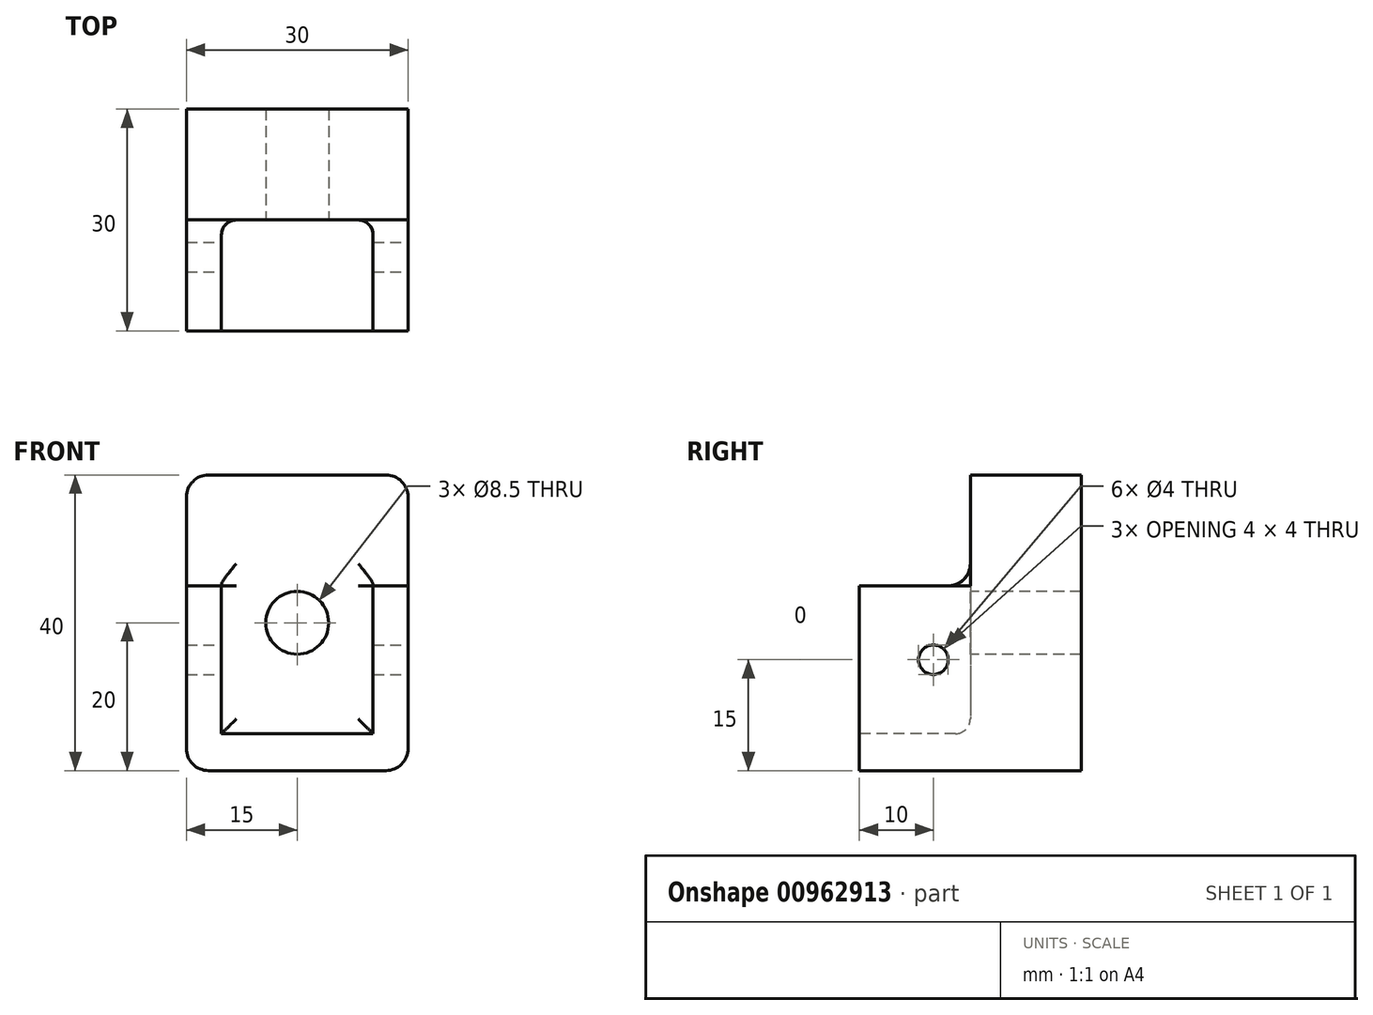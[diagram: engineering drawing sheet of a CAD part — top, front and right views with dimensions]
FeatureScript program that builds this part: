
annotation { "Feature Type Name" : "Feature", "Feature Type Description" : "" }
export const myFeature = defineFeature(function(context is Context, id is Id, definition is map)
    precondition{}
    {
        {
            var Q0;
            Q0=qCreatedBy(makeId("Front.planeOp"),FACE);
            var sketch = newSketch(context, id + "F0", { "sketchPlane" : qUnion([Q0])});
            skLineSegment(sketch, "E0.bottom", {"start": v(-15, 20) * mm, "end": v(15, 20) * mm});
            skLineSegment(sketch, "E0.top", {"start": v(-15, -20) * mm, "end": v(15, -20) * mm});
            skLineSegment(sketch, "E0.left", {"start": v(-15, 20) * mm, "end": v(-15, -20) * mm});
            skLineSegment(sketch, "E0.right", {"start": v(15, 20) * mm, "end": v(15, -20) * mm});
            skPoint(sketch, "E0.middle", {"position": v(0, 0) * mm});
            skSolve(sketch);
        }
        {
            var Q0;
            Q0 = qSketchRegion(id + "F0", true);
            extrude(context, id + "F1", {"entities" : qUnion([Q0]), "depth" : 30 * mm, "offsetDistance" : 25 * mm});
        }
        {
            var Q0;
            Q0=makeQuery(id+"F1.opExtrude","CAP_FACE",FACE,{"disambiguationData":[OSD([sQuery(id+"F0.wireOp",EDGE,"E0.bottom"),sQuery(id+"F0.wireOp",EDGE,"E0.top"),sQuery(id+"F0.wireOp",EDGE,"E0.left"),sQuery(id+"F0.wireOp",EDGE,"E0.right")])],"isStart":false});
            var sketch = newSketch(context, id + "F2", { "sketchPlane" : qUnion([Q0])});
            skLineSegment(sketch, "E1.bottom", {"start": v(-10.25, 15) * mm, "end": v(10.25, 15) * mm});
            skLineSegment(sketch, "E1.top", {"start": v(-10.25, -15) * mm, "end": v(10.25, -15) * mm});
            skLineSegment(sketch, "E1.left", {"start": v(-10.25, 15) * mm, "end": v(-10.25, -15) * mm});
            skLineSegment(sketch, "E1.right", {"start": v(10.25, 15) * mm, "end": v(10.25, -15) * mm});
            skPoint(sketch, "E1.middle", {"position": v(0, 0) * mm});
            skSolve(sketch);
        }
        {
            var Q0;
            Q0 = qSketchRegion(id + "F2", true);
            extrude(context, id + "F3", {"entities" : qUnion([Q0]), "operationType" : NewBodyOperationType.REMOVE, "oppositeDirection" : true, "depth" : 15 * mm, "offsetDistance" : 25 * mm});
        }
        {
            var Q0;
            Q0=makeQuery(id+"F1.opExtrude","CAP_FACE",FACE,{"disambiguationData":[OSD([sQuery(id+"F0.wireOp",EDGE,"E0.bottom"),sQuery(id+"F0.wireOp",EDGE,"E0.top"),sQuery(id+"F0.wireOp",EDGE,"E0.left"),sQuery(id+"F0.wireOp",EDGE,"E0.right")])],"isStart":false});
            var sketch = newSketch(context, id + "F4", { "sketchPlane" : qUnion([Q0])});
            skLineSegment(sketch, "E2.bottom", {"start": v(-15, 20) * mm, "end": v(19.05, 20) * mm});
            skLineSegment(sketch, "E2.top", {"start": v(-15, 5) * mm, "end": v(19.05, 5) * mm});
            skLineSegment(sketch, "E2.left", {"start": v(-15, 20) * mm, "end": v(-15, 5) * mm});
            skLineSegment(sketch, "E2.right", {"start": v(19.05, 20) * mm, "end": v(19.05, 5) * mm});
            skSolve(sketch);
        }
        {
            var Q0;
            Q0 = qSketchRegion(id + "F4", true);
            extrude(context, id + "F5", {"entities" : qUnion([Q0]), "operationType" : NewBodyOperationType.REMOVE, "oppositeDirection" : true, "depth" : 15 * mm, "offsetDistance" : 25 * mm});
        }
        {
            var Q0;
            Q0=makeQuery(id+"F5.boolean.opBoolean","MERGE",FACE,{"derivedFrom":[makeQuery(id+"F3.boolean.opBoolean","COPY",FACE,{"derivedFrom":makeQuery(id+"F3.opExtrude","CAP_FACE",FACE,{"disambiguationData":[OSD([sQuery(id+"F2.wireOp",EDGE,"E1.bottom"),sQuery(id+"F2.wireOp",EDGE,"E1.top"),sQuery(id+"F2.wireOp",EDGE,"E1.left"),sQuery(id+"F2.wireOp",EDGE,"E1.right")])],"isStart":false})})],"fromTools":[makeQuery(id+"F5.opExtrude","CAP_FACE",FACE,{"disambiguationData":[OSD([sQuery(id+"F4.wireOp",EDGE,"E2.bottom"),sQuery(id+"F4.wireOp",EDGE,"E2.top"),sQuery(id+"F4.wireOp",EDGE,"E2.left"),sQuery(id+"F4.wireOp",EDGE,"E2.right")])],"isStart":false})]});
            var sketch = newSketch(context, id + "F6", { "sketchPlane" : qUnion([Q0])});
            skCircle(sketch, "E3", {"center": v(0, 0) * mm, "radius": 4.25 * mm});
            skSolve(sketch);
        }
        {
            var Q0;
            Q0 = qSketchRegion(id + "F6", true);
            extrude(context, id + "F7", {"entities" : qUnion([Q0]), "operationType" : NewBodyOperationType.REMOVE, "oppositeDirection" : true, "depth" : 25 * mm, "offsetDistance" : 25 * mm});
        }
        {
            var Q0;
            Q0=makeQuery(id+"F1.opExtrude","SWEPT_FACE",FACE,{"disambiguationData":[OSD([sQuery(id+"F0.wireOp",EDGE,"E0.right")])]});
            var sketch = newSketch(context, id + "F8", { "sketchPlane" : qUnion([Q0])});
            skPoint(sketch, "E4", {"position": v(-20, -5) * mm});
            skCircle(sketch, "E5", {"center": v(-20, -5) * mm, "radius": 2 * mm});
            skSolve(sketch);
        }
        {
            var Q0;
            Q0 = qSketchRegion(id + "F8", true);
            extrude(context, id + "F9", {"entities" : qUnion([Q0]), "operationType" : NewBodyOperationType.REMOVE, "endBound" : BoundingType.THROUGH_ALL, "oppositeDirection" : true, "depth" : 25 * mm, "offsetDistance" : 25 * mm});
        }
        {
            var Q0;
            Q0=makeQuery(id+"F1.opExtrude","SWEPT_EDGE",EDGE,{"disambiguationData":[OSD([sQuery(id+"F0.wireOp",EDGE,"E0.bottom"),sQuery(id+"F0.wireOp",EDGE,"E0.right")])]});
            var Q1;
            {var subQ0=sQuery(id+"F0.wireOp",EDGE,"E0.right");var subQ1=sQuery(id+"F4.wireOp",EDGE,"E2.top");Q1=makeQuery(id+"F5.boolean.opBoolean","COPY",EDGE,{"disambiguationData":[TD([makeQuery(id+"F1.opExtrude","SWEPT_FACE",FACE,{"disambiguationData":[OSD([subQ0])]})])],"derivedFrom":makeQuery(id+"F5.opExtrude","CAP_EDGE",EDGE,{"disambiguationData":[OSD([subQ1])],"isStart":true})});}
            var Q2;
            {var subQ0=sQuery(id+"F0.wireOp",EDGE,"E0.left");var subQ1=sQuery(id+"F4.wireOp",EDGE,"E2.top");Q2=makeQuery(id+"F5.boolean.opBoolean","COPY",EDGE,{"disambiguationData":[TD([makeQuery(id+"F1.opExtrude","SWEPT_FACE",FACE,{"disambiguationData":[OSD([subQ0])]})])],"derivedFrom":makeQuery(id+"F5.opExtrude","CAP_EDGE",EDGE,{"disambiguationData":[OSD([subQ1])],"isStart":true})});}
            var Q3;
            {var subQ0=sQuery(id+"F4.wireOp",EDGE,"E2.top");Q3=makeQuery(id+"F5.boolean.opBoolean","COPY",EDGE,{"disambiguationData":[TD([makeQuery(id+"F1.opExtrude","SWEPT_FACE",FACE,{"disambiguationData":[OSD([sQuery(id+"F0.wireOp",EDGE,"E0.right")])]})])],"derivedFrom":makeQuery(id+"F5.opExtrude","CAP_EDGE",EDGE,{"disambiguationData":[OSD([subQ0])],"isStart":false})});}
            var Q4;
            {var subQ1=sQuery(id+"F4.wireOp",EDGE,"E2.top");Q4=makeQuery(id+"F5.boolean.opBoolean","COPY",EDGE,{"disambiguationData":[TD([makeQuery(id+"F1.opExtrude","SWEPT_FACE",FACE,{"disambiguationData":[OSD([sQuery(id+"F0.wireOp",EDGE,"E0.left")])]})])],"derivedFrom":makeQuery(id+"F5.opExtrude","CAP_EDGE",EDGE,{"disambiguationData":[OSD([subQ1])],"isStart":false})});}
            var Q5;
            Q5=makeQuery(id+"F1.opExtrude","SWEPT_EDGE",EDGE,{"disambiguationData":[OSD([sQuery(id+"F0.wireOp",EDGE,"E0.bottom"),sQuery(id+"F0.wireOp",EDGE,"E0.left")])]});
            var Q6;
            Q6=makeQuery(id+"F1.opExtrude","SWEPT_EDGE",EDGE,{"disambiguationData":[OSD([sQuery(id+"F0.wireOp",EDGE,"E0.top"),sQuery(id+"F0.wireOp",EDGE,"E0.left")])]});
            var Q7;
            Q7=makeQuery(id+"F1.opExtrude","SWEPT_EDGE",EDGE,{"disambiguationData":[OSD([sQuery(id+"F0.wireOp",EDGE,"E0.top"),sQuery(id+"F0.wireOp",EDGE,"E0.right")])]});
            fillet(context, id + "F10", {"entities" : qUnion([Q0, Q1, Q2, Q3, Q4, Q5, Q6, Q7]), "radius" : 3 * mm, "tangentPropagation" : true, "allowEdgeOverflow" : false});
        }
        {
            var Q0;
            Q0=makeQuery(id+"F3.boolean.opBoolean","COPY",EDGE,{"derivedFrom":makeQuery(id+"F3.opExtrude","CAP_EDGE",EDGE,{"disambiguationData":[OSD([sQuery(id+"F2.wireOp",EDGE,"E1.left")])],"isStart":false})});
            var Q1;
            Q1=makeQuery(id+"F3.boolean.opBoolean","COPY",EDGE,{"derivedFrom":makeQuery(id+"F3.opExtrude","CAP_EDGE",EDGE,{"disambiguationData":[OSD([sQuery(id+"F2.wireOp",EDGE,"E1.top")])],"isStart":false})});
            var Q2;
            Q2=makeQuery(id+"F3.boolean.opBoolean","COPY",EDGE,{"derivedFrom":makeQuery(id+"F3.opExtrude","CAP_EDGE",EDGE,{"disambiguationData":[OSD([sQuery(id+"F2.wireOp",EDGE,"E1.right")])],"isStart":false})});
            fillet(context, id + "F11", {"entities" : qUnion([Q0, Q1, Q2]), "radius" : 2 * mm, "tangentPropagation" : true, "allowEdgeOverflow" : false});
        }
    });
